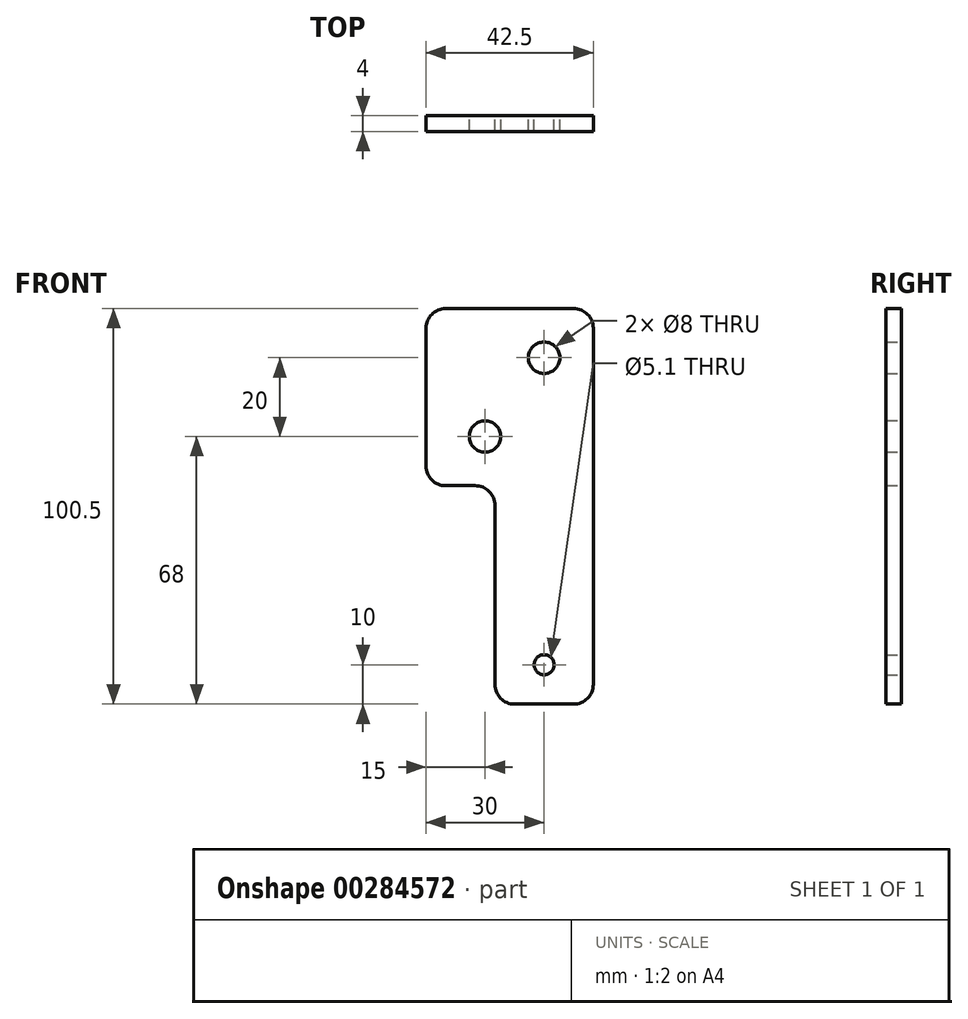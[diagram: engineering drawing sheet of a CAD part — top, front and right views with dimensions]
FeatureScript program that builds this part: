
annotation { "Feature Type Name" : "Feature", "Feature Type Description" : "" }
export const myFeature = defineFeature(function(context is Context, id is Id, definition is map)
    precondition{}
    {
        {
            var Q0;
            Q0=qCreatedBy(makeId("Front.planeOp"),FACE);
            var sketch = newSketch(context, id + "F0", { "sketchPlane" : qUnion([Q0])});
            skLineSegment(sketch, "E0", {"start": v(0, 5) * mm, "end": v(0, 50.5) * mm});
            skLineSegment(sketch, "E1", {"start": v(-5, 55.5) * mm, "end": v(-12.5, 55.5) * mm});
            skLineSegment(sketch, "E2", {"start": v(-17.5, 60.5) * mm, "end": v(-17.5, 95.5) * mm});
            skLineSegment(sketch, "E3", {"start": v(-12.5, 100.5) * mm, "end": v(20, 100.5) * mm});
            skLineSegment(sketch, "E4", {"start": v(25, 95.5) * mm, "end": v(25, 5) * mm});
            skLineSegment(sketch, "E5", {"start": v(20, 0) * mm, "end": v(5, 0) * mm});
            skPoint(sketch, "E6", {"position": v(12.5, 10) * mm});
            skPoint(sketch, "E7", {"position": v(12.5, 88) * mm});
            skPoint(sketch, "E8", {"position": v(-2.5, 68) * mm});
            skPoint(sketch, "E9.visualSharp", {"position": v(-17.5, 100.5) * mm});
            skArc(sketch, "E9.filletArc", {"start": v(-12.5, 100.5) * mm, "mid": v(-16.04, 99.04) * mm, "end": v(-17.5, 95.5) * mm});
            skPoint(sketch, "E10.visualSharp", {"position": v(25, 100.5) * mm});
            skArc(sketch, "E10.filletArc", {"start": v(25, 95.5) * mm, "mid": v(23.54, 99.04) * mm, "end": v(20, 100.5) * mm});
            skPoint(sketch, "E11.visualSharp", {"position": v(-17.5, 55.5) * mm});
            skArc(sketch, "E11.filletArc", {"start": v(-17.5, 60.5) * mm, "mid": v(-16.04, 56.96) * mm, "end": v(-12.5, 55.5) * mm});
            skPoint(sketch, "E12.visualSharp", {"position": v(0, 55.5) * mm});
            skArc(sketch, "E12.filletArc", {"start": v(0, 50.5) * mm, "mid": v(-1.46, 54.04) * mm, "end": v(-5, 55.5) * mm});
            skPoint(sketch, "E13.visualSharp", {"position": v(0, 0) * mm});
            skArc(sketch, "E13.filletArc", {"start": v(0, 5) * mm, "mid": v(1.46, 1.46) * mm, "end": v(5, 0) * mm});
            skPoint(sketch, "E14.visualSharp", {"position": v(25, 0) * mm});
            skArc(sketch, "E14.filletArc", {"start": v(20, 0) * mm, "mid": v(23.54, 1.46) * mm, "end": v(25, 5) * mm});
            skCircle(sketch, "E15", {"center": v(-2.5, 68) * mm, "radius": 4 * mm});
            skCircle(sketch, "E16", {"center": v(12.5, 88) * mm, "radius": 4 * mm});
            skCircle(sketch, "E17", {"center": v(12.5, 10) * mm, "radius": 2.55 * mm});
            skSolve(sketch);
        }
        {
            var Q0;
            Q0=qSketchRegion(id+"F0",true);
            extrude(context, id + "F1", {"entities" : qUnion([Q0]), "depth" : 4 * mm});
        }
    });
